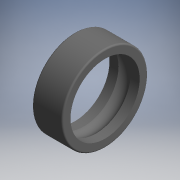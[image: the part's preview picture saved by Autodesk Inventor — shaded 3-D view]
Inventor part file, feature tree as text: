
AUTODESK INVENTOR PART (.ipt)
format: ipt  version: 2017.3 (Build 213256000, 256)  size: 129,024 bytes
history: native  units: mm (DEFAULTED — no unit token found)
features: other x7, revolve x1, sketch x1
ambient origin geometry x8: Origin, YZ Plane, XZ Plane, XY Plane, X Axis, Y Axis, Z Axis, Center Point
bodies: Solid1 (feature_tree)
feature tree (9):
  revolve  "Revolution1"  [1 undecoded]
  other  "ip_ot_or_XY"
  other  "ip_ot_or_YZ"
  other  "ip_ot_or_ZX"
  other  "ip_ot_or_X"
  other  "ip_ot_or_Y"
  other  "ip_ot_or_Z"
  other  "ip_ot_or_Center"
  sketch  "Sketch_1"  dims[d0=360.0deg d1=0.0mm]
note: 1 required parameter value undecoded (feature->parameter linkage not recoverable at this tier; creation-order binding heuristic only, values carry confidence <= 0.55)
